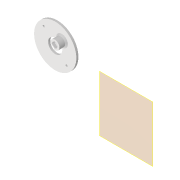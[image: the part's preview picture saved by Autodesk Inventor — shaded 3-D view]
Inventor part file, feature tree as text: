
AUTODESK INVENTOR PART (.ipt)
format: ipt  version: 2022 (Build 260153000, 153)  size: 220,160 bytes
history: native  units: in
note: dims shown in document units (in); Inventor stores cm internally (conversion verified against a paired STEP export)
features: reference x24, other x8, extrude x6, sketch x5, projected_geometry x3, plane x1, chamfer x1
ambient origin geometry x8: Origin, YZ Plane, XZ Plane, XY Plane, X Axis, Y Axis, Z Axis, Center Point
bodies: Volumenkörper1 (feature_tree)
feature tree (48):
  other  "00_toslink_launcher_v3.ipt"
  plane  "Arbeitsebene1"
  extrude  "Extrusion1"  Depth=0.1181in TaperAngle=0.0deg
  extrude  "Extrusion4"  Depth=0.3937in
  extrude  "Extrusion5"  Depth=0.3937in TaperAngle=0.0deg
  extrude  "Extrusion6"  Depth=2.3622in
  extrude  "Extrusion7"  Depth=0.0394in TaperAngle=0.0deg
  chamfer  "Chamfer1"  Distance=0.0787in Angle=45.0deg
  extrude  "Extrusion8"  TaperAngle=45.0deg  [1 undecoded]
  reference  "Referenz1"
  reference  "Reference2"
  reference  "Reference3"
  sketch  "Sketch4"  dims[d0=0.7874in d1=0.1181in d2=0.0in]
  reference  "Reference4"
  sketch  "Sketch6"  dims[d13=0.3937in d14=0.0in d16=0.3937in]
  reference  "Reference7"
  reference  "Reference8"
  reference  "Reference9"
  reference  "Reference10"
  reference  "Reference11"
  reference  "Reference12"
  reference  "Reference13"
  reference  "Reference14"
  reference  "Reference15"
  projected_geometry  "Projected Loop5"
  reference  "Reference16"
  reference  "Reference17"
  reference  "Reference18"
  reference  "Reference19"
  reference  "Reference20"
  reference  "Reference21"
  reference  "Reference22"
  reference  "Reference23"
  reference  "Reference24"
  reference  "Reference25"
  sketch  "Sketch7"  dims[d17=0.5118in d18=0.3937in d19=0.0in]
  sketch  "Sketch8"  dims[d20=0.2362in d21=2.3622in]
  projected_geometry  "Projected Loop6"
  sketch  "Sketch9"  dims[d22=0.0394in d23=0.0in d24=0.0394in d25=0.0in d26=0.0787in d27=0.0787in d28=45.0deg d29=45.0deg d30=0.0in d31=0.1102in d32=0.1102in d33=0.0in d34=0.0in d35=1.4173in]
  reference  "Reference26"
  projected_geometry  "Projected Loop7"
  other  "Anglerfish_bonne_mamman_v0.iam"
  other  "00_bonne_maman_jar:1"
  other  "00_ESP3-CAM:1"
  other  "Bauteil50"
  other  "00_toslink_launcher_v3:1"
  other  "Matchboxscope_M12_Lensadapter_v0:1"
  other  "Anglerfish_Jar_Adapterplate_v1:1"
note: 1 required parameter value undecoded (feature->parameter linkage not recoverable at this tier; creation-order binding heuristic only, values carry confidence <= 0.55)
